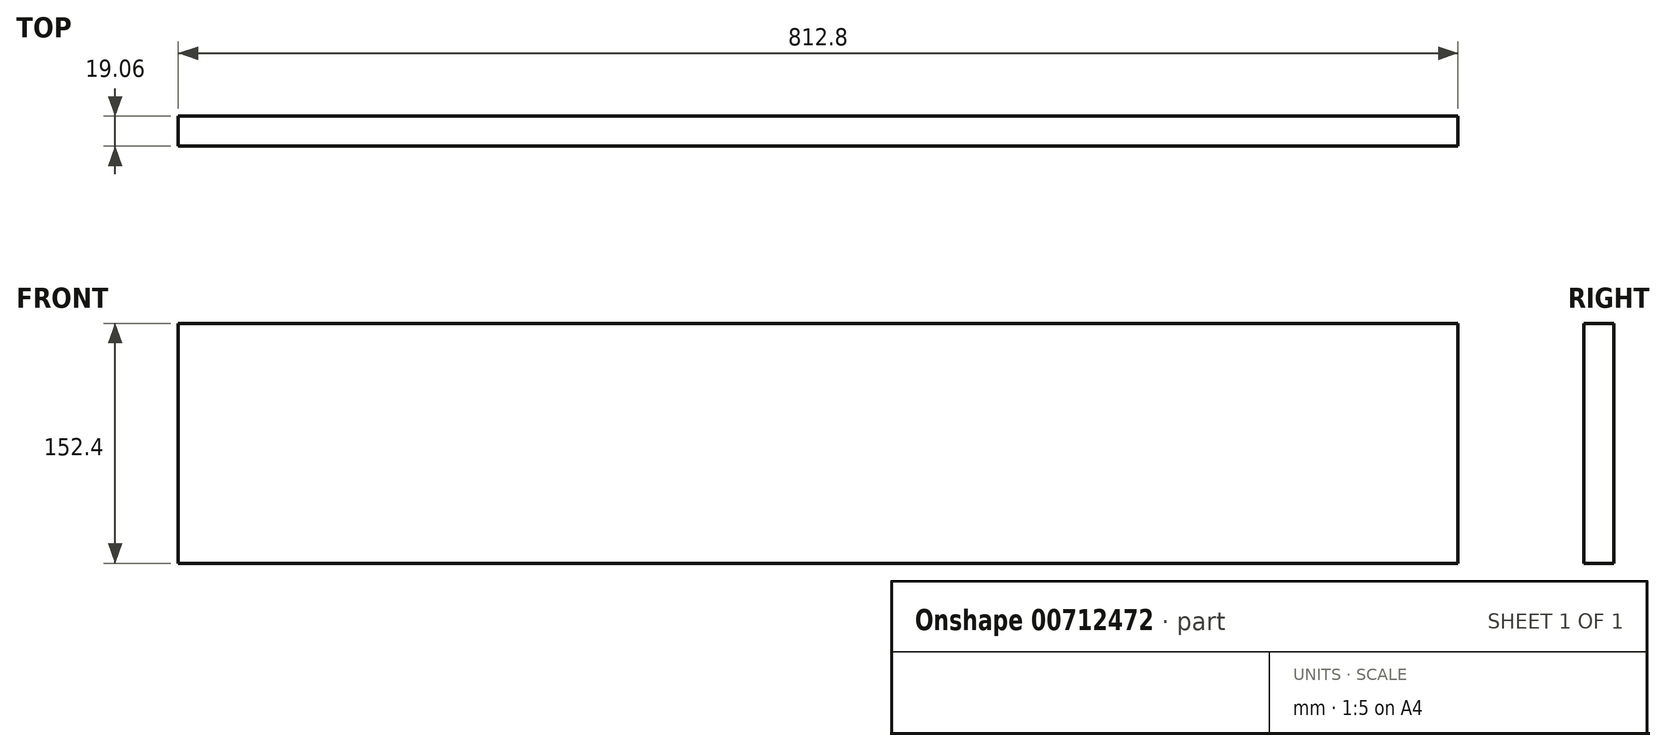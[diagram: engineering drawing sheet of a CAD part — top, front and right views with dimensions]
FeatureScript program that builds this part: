
annotation { "Feature Type Name" : "Feature", "Feature Type Description" : "" }
export const myFeature = defineFeature(function(context is Context, id is Id, definition is map)
    precondition{}
    {
        {
            var Q0;
            Q0=qCreatedBy(makeId("Front.planeOp"),FACE);
            var sketch = newSketch(context, id + "F0", { "sketchPlane" : qUnion([Q0])});
            skLineSegment(sketch, "E0.bottom", {"start": v(-406.4, 76.2) * mm, "end": v(406.4, 76.2) * mm});
            skLineSegment(sketch, "E0.top", {"start": v(-406.4, -76.2) * mm, "end": v(406.4, -76.2) * mm});
            skLineSegment(sketch, "E0.left", {"start": v(-406.4, 76.2) * mm, "end": v(-406.4, -76.2) * mm});
            skLineSegment(sketch, "E0.right", {"start": v(406.4, 76.2) * mm, "end": v(406.4, -76.2) * mm});
            skPoint(sketch, "E0.middle", {"position": v(0, 0) * mm});
            skSolve(sketch);
        }
        {
            var Q0;
            Q0=makeQuery(id+"F0.imprint","IMPRINT",FACE,{"disambiguationData":[TD([[makeQuery(id+"F0.imprint","IMPRINT",EDGE,{"derivedFrom":sQuery(id+"F0.wireOp",EDGE,"E0.bottom")}),-1.0]])]});
            extrude(context, id + "F1", {"entities" : qUnion([Q0]), "endBound" : BoundingType.SYMMETRIC, "depth" : 19.05 * mm, "offsetDistance" : 25.4 * mm});
        }
    });
